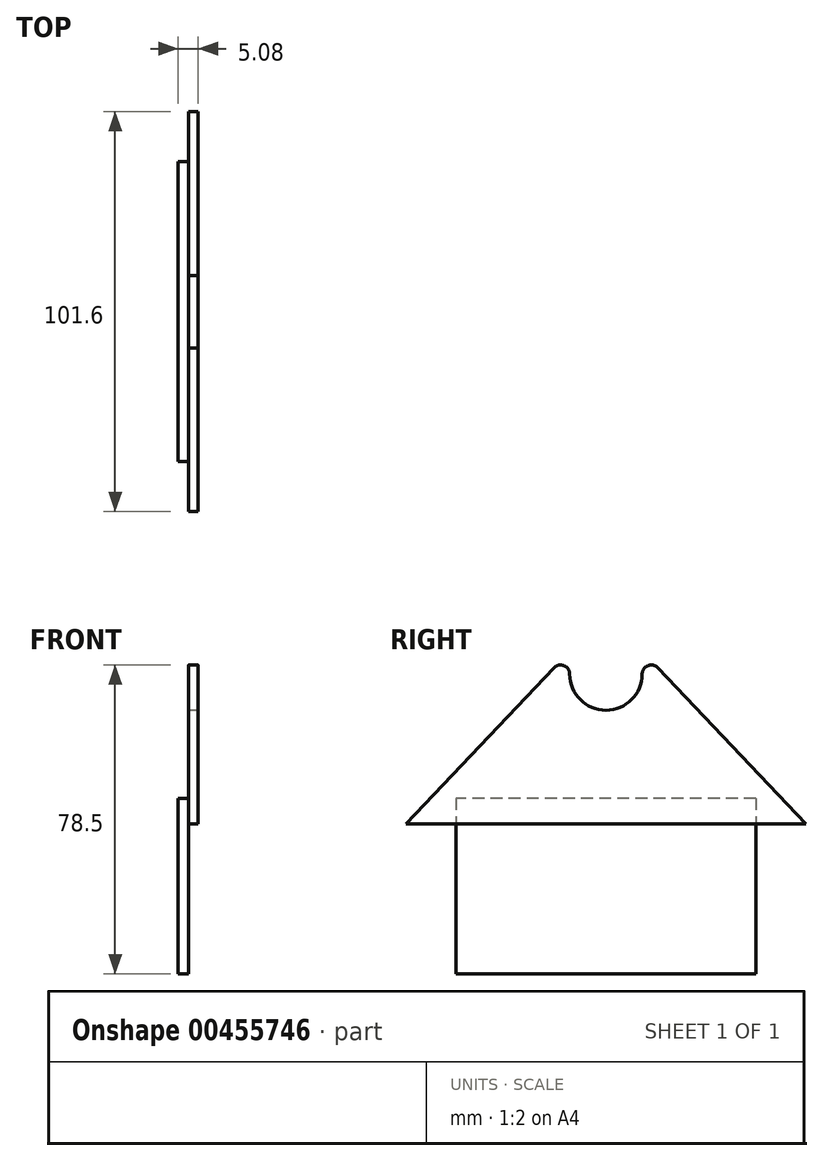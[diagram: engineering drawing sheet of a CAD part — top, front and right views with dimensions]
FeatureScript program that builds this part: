
annotation { "Feature Type Name" : "Feature", "Feature Type Description" : "" }
export const myFeature = defineFeature(function(context is Context, id is Id, definition is map)
    precondition{}
    {
        {
            var Q0;
            Q0=qCreatedBy(makeId("Right.planeOp"),FACE);
            var sketch = newSketch(context, id + "F0", { "sketchPlane" : qUnion([Q0])});
            skLineSegment(sketch, "E0", {"start": v(-50.8, 0) * mm, "end": v(50.8, 0) * mm});
            skArc(sketch, "E1", {"start": v(-9.2, 38.1) * mm, "mid": v(0, 28.9) * mm, "end": v(9.2, 38.1) * mm});
            skArc(sketch, "E2", {"start": v(-9.2, 38.1) * mm, "mid": v(-10.66, 40.24) * mm, "end": v(-13.18, 39.68) * mm});
            skLineSegment(sketch, "E3", {"start": v(-50.8, 0) * mm, "end": v(-13.18, 39.68) * mm});
            skLineSegment(sketch, "E4", {"start": v(0, 0) * mm, "end": v(0, 52.92) * mm, "construction": true});
            skArc(sketch, "E5.MirrorC", {"start": v(9.2, 38.1) * mm, "mid": v(10.66, 40.24) * mm, "end": v(13.18, 39.68) * mm});
            skLineSegment(sketch, "E6.MirrorCS", {"start": v(50.8, 0) * mm, "end": v(13.18, 39.68) * mm});
            skSolve(sketch);
        }
        {
            var Q0;
            Q0 = qSketchRegion(id + "F0", true);
            extrude(context, id + "F1", {"entities" : qUnion([Q0]), "depth" : 2.54 * mm});
        }
        {
            var Q0;
            Q0=qCreatedBy(makeId("Right.planeOp"),FACE);
            var sketch = newSketch(context, id + "F2", { "sketchPlane" : qUnion([Q0])});
            skLineSegment(sketch, "E7.bottom", {"start": v(38.1, 6.53) * mm, "end": v(-38.1, 6.53) * mm});
            skLineSegment(sketch, "E7.top", {"start": v(38.1, -38.1) * mm, "end": v(-38.1, -38.1) * mm});
            skLineSegment(sketch, "E7.left", {"start": v(38.1, 6.53) * mm, "end": v(38.1, -38.1) * mm});
            skLineSegment(sketch, "E7.right", {"start": v(-38.1, 6.53) * mm, "end": v(-38.1, -38.1) * mm});
            skSolve(sketch);
        }
        {
            var Q0;
            Q0 = qSketchRegion(id + "F2", true);
            extrude(context, id + "F3", {"entities" : qUnion([Q0]), "operationType" : NewBodyOperationType.ADD, "oppositeDirection" : true, "depth" : 2.54 * mm});
        }
    });
